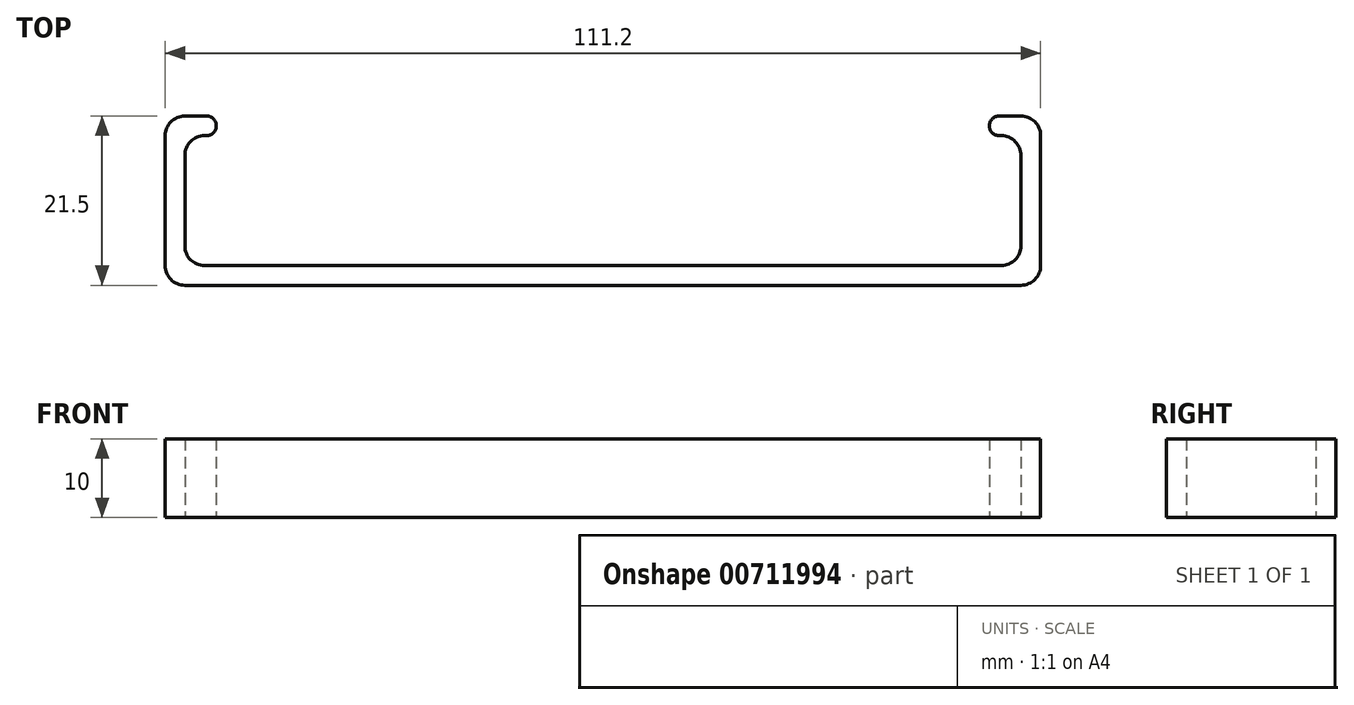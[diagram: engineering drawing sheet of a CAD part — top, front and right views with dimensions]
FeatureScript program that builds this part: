
annotation { "Feature Type Name" : "Feature", "Feature Type Description" : "" }
export const myFeature = defineFeature(function(context is Context, id is Id, definition is map)
    precondition{}
    {
        {
            var Q0;
            Q0=qCreatedBy(makeId("Top.planeOp"),FACE);
            var sketch = newSketch(context, id + "F0", { "sketchPlane" : qUnion([Q0])});
            skLineSegment(sketch, "E0", {"start": v(0, 0) * mm, "end": v(-50.6, 0) * mm});
            skLineSegment(sketch, "E1", {"start": v(-53.1, 2.5) * mm, "end": v(-53.1, 14) * mm});
            skPoint(sketch, "E2.MirrorCS.end.orphan", {"position": v(53.1, 0) * mm});
            skPoint(sketch, "E2.MirrorCS.start.orphan", {"position": v(0, 0) * mm});
            skLineSegment(sketch, "E3.MirrorCS", {"start": v(0, 0) * mm, "end": v(50.6, 0) * mm});
            skLineSegment(sketch, "E4.MirrorCS", {"start": v(53.1, 2.5) * mm, "end": v(53.1, 14) * mm});
            skLineSegment(sketch, "E5", {"start": v(-50.6, 16.5) * mm, "end": v(-50.35, 16.5) * mm});
            skLineSegment(sketch, "E6.MirrorCS", {"start": v(50.6, 16.5) * mm, "end": v(50.35, 16.5) * mm});
            skLineSegment(sketch, "E7.0", {"start": v(-53.1, 19) * mm, "end": v(-50.35, 19) * mm});
            skLineSegment(sketch, "E8.0", {"start": v(-55.6, 0) * mm, "end": v(-55.6, 16.5) * mm});
            skLineSegment(sketch, "E9.0", {"start": v(0, -2.5) * mm, "end": v(-53.1, -2.5) * mm});
            skLineSegment(sketch, "E10.0", {"start": v(0, -2.5) * mm, "end": v(53.1, -2.5) * mm});
            skLineSegment(sketch, "E11.0", {"start": v(55.6, 0) * mm, "end": v(55.6, 16.5) * mm});
            skLineSegment(sketch, "E12.0", {"start": v(53.1, 19) * mm, "end": v(50.35, 19) * mm});
            skLineSegment(sketch, "E13", {"start": v(53.1, -2.5) * mm, "end": v(53.1, -2.5) * mm});
            skLineSegment(sketch, "E14", {"start": v(55.6, 0) * mm, "end": v(55.6, 0) * mm});
            skLineSegment(sketch, "E15", {"start": v(-55.6, 0) * mm, "end": v(-55.6, 0) * mm});
            skLineSegment(sketch, "E16", {"start": v(-53.1, -2.5) * mm, "end": v(-53.1, -2.5) * mm});
            skLineSegment(sketch, "E17", {"start": v(-53.1, 19) * mm, "end": v(-53.1, 19) * mm});
            skLineSegment(sketch, "E18", {"start": v(-55.6, 16.5) * mm, "end": v(-55.6, 16.5) * mm});
            skLineSegment(sketch, "E19", {"start": v(-49.1, 17.75) * mm, "end": v(-50.35, 17.75) * mm, "construction": true});
            skLineSegment(sketch, "E20", {"start": v(-50.35, 19) * mm, "end": v(-50.35, 16.5) * mm, "construction": true});
            skArc(sketch, "E21", {"start": v(-50.35, 16.5) * mm, "mid": v(-49.1, 17.75) * mm, "end": v(-50.35, 19) * mm});
            skPoint(sketch, "E22.orphan", {"position": v(-49.1, 16.5) * mm});
            skPoint(sketch, "E23.orphan", {"position": v(-49.1, 19) * mm});
            skPoint(sketch, "E24.visualSharp", {"position": v(-55.6, 19) * mm});
            skArc(sketch, "E24.filletArc", {"start": v(-53.1, 19) * mm, "mid": v(-54.87, 18.27) * mm, "end": v(-55.6, 16.5) * mm});
            skArc(sketch, "E25.filletArc", {"start": v(-50.6, 16.5) * mm, "mid": v(-52.37, 15.77) * mm, "end": v(-53.1, 14) * mm});
            skPoint(sketch, "E26.visualSharp", {"position": v(-50.78, 18.75) * mm});
            skPoint(sketch, "E27.visualSharp", {"position": v(-53.1, 18.75) * mm});
            skPoint(sketch, "E28.visualSharp", {"position": v(-55.6, -2.5) * mm});
            skArc(sketch, "E28.filletArc", {"start": v(-55.6, 0) * mm, "mid": v(-54.87, -1.77) * mm, "end": v(-53.1, -2.5) * mm});
            skArc(sketch, "E29.filletArc", {"start": v(-53.1, 2.5) * mm, "mid": v(-52.37, 0.73) * mm, "end": v(-50.6, 0) * mm});
            skArc(sketch, "E30.filletArc", {"start": v(50.6, 0) * mm, "mid": v(52.37, 0.73) * mm, "end": v(53.1, 2.5) * mm});
            skPoint(sketch, "E31.visualSharp", {"position": v(55.6, -2.5) * mm});
            skArc(sketch, "E31.filletArc", {"start": v(53.1, -2.5) * mm, "mid": v(54.87, -1.77) * mm, "end": v(55.6, 0) * mm});
            skPoint(sketch, "E32.visualSharp", {"position": v(55.6, 19) * mm});
            skArc(sketch, "E32.filletArc", {"start": v(55.6, 16.5) * mm, "mid": v(54.87, 18.27) * mm, "end": v(53.1, 19) * mm});
            skArc(sketch, "E33.filletArc", {"start": v(53.1, 14) * mm, "mid": v(52.37, 15.77) * mm, "end": v(50.6, 16.5) * mm});
            skLineSegment(sketch, "E34", {"start": v(49.1, 17.75) * mm, "end": v(50.35, 17.75) * mm, "construction": true});
            skLineSegment(sketch, "E35", {"start": v(50.35, 19) * mm, "end": v(50.35, 16.5) * mm, "construction": true});
            skArc(sketch, "E36", {"start": v(50.35, 19) * mm, "mid": v(49.1, 17.75) * mm, "end": v(50.35, 16.5) * mm});
            skPoint(sketch, "E37.orphan", {"position": v(49.1, 16.5) * mm});
            skPoint(sketch, "E38.orphan", {"position": v(49.1, 19) * mm});
            skSolve(sketch);
        }
        {
            var Q0;
            Q0 = qSketchRegion(id + "F0", true);
            extrude(context, id + "F1", {"entities" : qUnion([Q0]), "depth" : 10 * mm, "offsetDistance" : 25 * mm});
        }
    });
